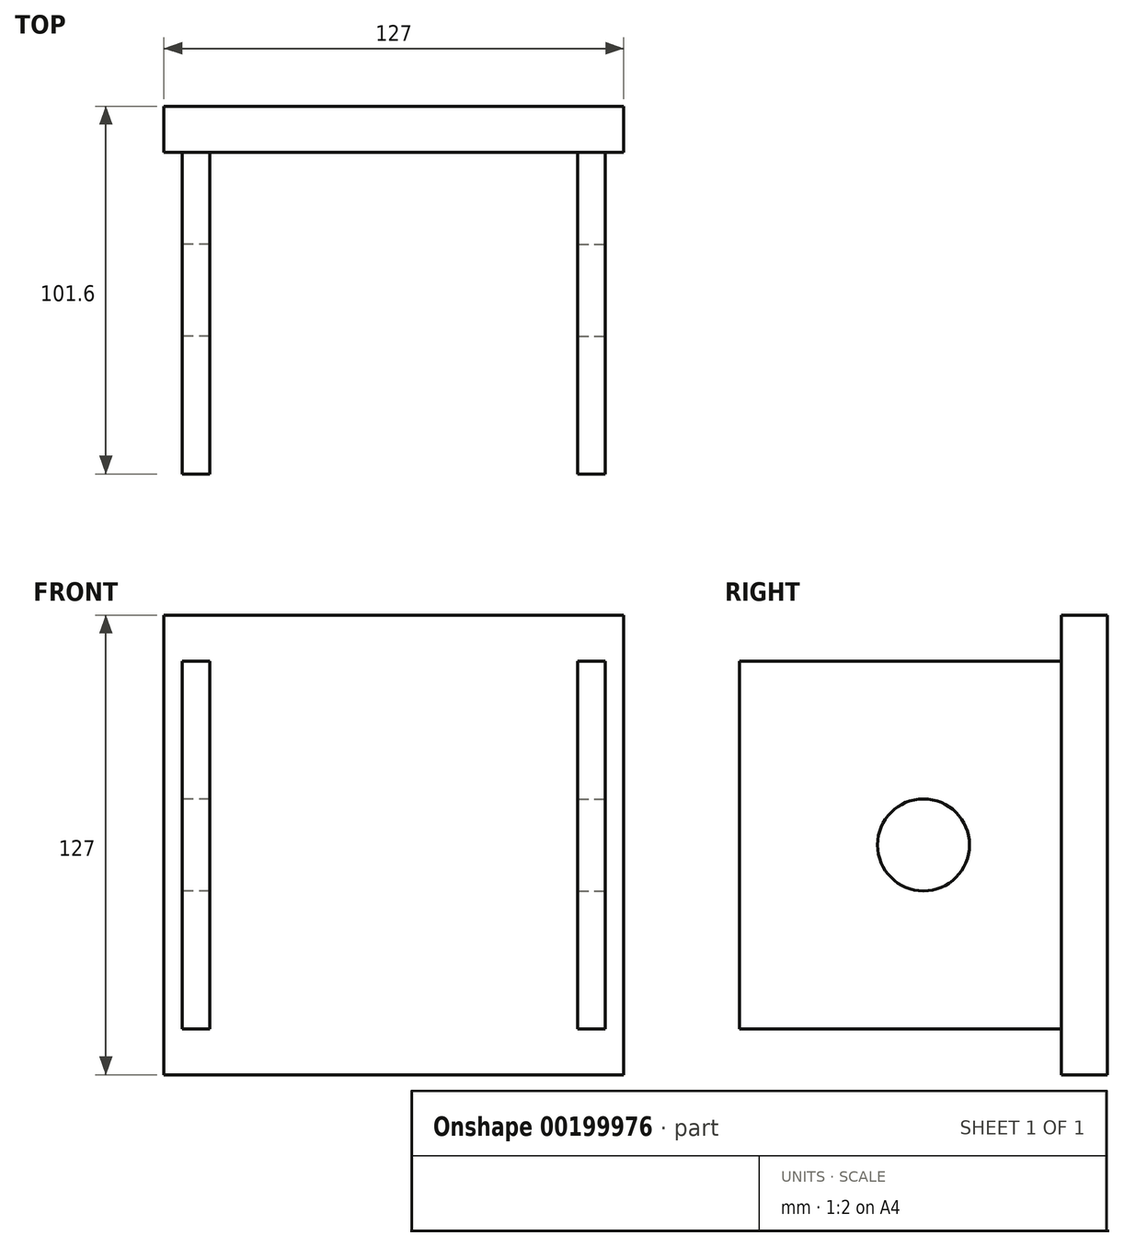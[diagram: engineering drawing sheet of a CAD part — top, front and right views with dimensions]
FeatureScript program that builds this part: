
annotation { "Feature Type Name" : "Feature", "Feature Type Description" : "" }
export const myFeature = defineFeature(function(context is Context, id is Id, definition is map)
    precondition{}
    {
        {
            var Q0;
            Q0=qCreatedBy(makeId("Front.planeOp"),FACE);
            var sketch = newSketch(context, id + "F0", { "sketchPlane" : qUnion([Q0])});
            skLineSegment(sketch, "E0.bottom", {"start": v(63.5, -63.5) * mm, "end": v(-63.5, -63.5) * mm});
            skLineSegment(sketch, "E0.top", {"start": v(63.5, 63.5) * mm, "end": v(-63.5, 63.5) * mm});
            skLineSegment(sketch, "E0.left", {"start": v(63.5, -63.5) * mm, "end": v(63.5, 63.5) * mm});
            skLineSegment(sketch, "E0.right", {"start": v(-63.5, -63.5) * mm, "end": v(-63.5, 63.5) * mm});
            skPoint(sketch, "E0.middle", {"position": v(0, 0) * mm});
            skLineSegment(sketch, "E1.bottom", {"start": v(-50.8, -50.8) * mm, "end": v(-58.42, -50.8) * mm});
            skLineSegment(sketch, "E1.top", {"start": v(-50.8, 50.8) * mm, "end": v(-58.42, 50.8) * mm});
            skLineSegment(sketch, "E1.left", {"start": v(-50.8, -50.8) * mm, "end": v(-50.8, 50.8) * mm});
            skLineSegment(sketch, "E1.right", {"start": v(-58.42, -50.8) * mm, "end": v(-58.42, 50.8) * mm});
            skPoint(sketch, "E1.middle", {"position": v(-54.6, 0) * mm});
            skSolve(sketch);
        }
        {
            var Q0;
            Q0=makeQuery(id+"F0.imprint","IMPRINT",FACE,{"disambiguationData":[TD([[makeQuery(id+"F0.imprint","IMPRINT",EDGE,{"derivedFrom":sQuery(id+"F0.wireOp",EDGE,"E1.bottom")}),-1.0]])]});
            extrude(context, id + "F1", {"entities" : qUnion([Q0]), "depth" : 101.6 * mm});
        }
        {
            var Q0;
            Q0=makeQuery(id+"F1.opExtrude","SWEPT_FACE",FACE,{"disambiguationData":[OSD([sQuery(id+"F0.wireOp",EDGE,"E1.right")])]});
            var sketch = newSketch(context, id + "F2", { "sketchPlane" : qUnion([Q0])});
            skCircle(sketch, "E2", {"center": v(50.8, 0) * mm, "radius": 12.7 * mm});
            skPoint(sketch, "E2.centerSnap0", {"position": v(0, 0) * mm});
            skSolve(sketch);
        }
        {
            var Q0;
            Q0=makeQuery(id+"F2.imprint","IMPRINT",FACE,{"disambiguationData":[TD([[makeQuery(id+"F2.imprint","IMPRINT",EDGE,{"derivedFrom":sQuery(id+"F2.wireOp",EDGE,"E2")}),1.0]])]});
            extrude(context, id + "F3", {"entities" : qUnion([Q0]), "operationType" : NewBodyOperationType.REMOVE, "endBound" : BoundingType.THROUGH_ALL, "oppositeDirection" : true, "depth" : 25.4 * mm});
        }
        {
            var Q0;
            Q0=makeQuery(id+"F0.imprint","IMPRINT",FACE,{"disambiguationData":[TD([[makeQuery(id+"F0.imprint","IMPRINT",EDGE,{"derivedFrom":sQuery(id+"F0.wireOp",EDGE,"E0.bottom")}),-1.0]])]});
            var sketch = newSketch(context, id + "F4", { "sketchPlane" : qUnion([Q0])});
            skLineSegment(sketch, "E3.bottom", {"start": v(58.42, 50.8) * mm, "end": v(50.8, 50.8) * mm});
            skLineSegment(sketch, "E3.top", {"start": v(58.42, -50.8) * mm, "end": v(50.8, -50.8) * mm});
            skLineSegment(sketch, "E3.left", {"start": v(58.42, 50.8) * mm, "end": v(58.42, -50.8) * mm});
            skLineSegment(sketch, "E3.right", {"start": v(50.8, 50.8) * mm, "end": v(50.8, -50.8) * mm});
            skPoint(sketch, "E3.middle", {"position": v(54.6, 0) * mm});
            skSolve(sketch);
        }
        {
            var Q0;
            Q0=qSketchRegion(id+"F4",true);
            extrude(context, id + "F5", {"entities" : qUnion([Q0]), "operationType" : NewBodyOperationType.ADD, "depth" : 101.6 * mm});
        }
        {
            var Q0;
            Q0=makeQuery(id+"F5.opExtrude","SWEPT_FACE",FACE,{"disambiguationData":[OSD([sQuery(id+"F4.wireOp",EDGE,"E3.left")])]});
            var sketch = newSketch(context, id + "F6", { "sketchPlane" : qUnion([Q0])});
            skCircle(sketch, "E4", {"center": v(-50.8, 0) * mm, "radius": 12.7 * mm});
            skSolve(sketch);
        }
        {
            var Q0;
            Q0=makeQuery(id+"F6.imprint","IMPRINT",FACE,{"disambiguationData":[TD([[makeQuery(id+"F6.imprint","IMPRINT",EDGE,{"derivedFrom":sQuery(id+"F6.wireOp",EDGE,"E4")}),1.0]])]});
            extrude(context, id + "F7", {"entities" : qUnion([Q0]), "operationType" : NewBodyOperationType.REMOVE, "endBound" : BoundingType.THROUGH_ALL, "oppositeDirection" : true, "depth" : 25.4 * mm});
        }
        {
            var Q0;
            Q0=makeQuery(id+"F0.imprint","IMPRINT",FACE,{"disambiguationData":[TD([[makeQuery(id+"F0.imprint","IMPRINT",EDGE,{"derivedFrom":sQuery(id+"F0.wireOp",EDGE,"E0.bottom")}),-1.0]])]});
            extrude(context, id + "F8", {"entities" : qUnion([Q0]), "operationType" : NewBodyOperationType.ADD, "depth" : 12.7 * mm});
        }
    });
